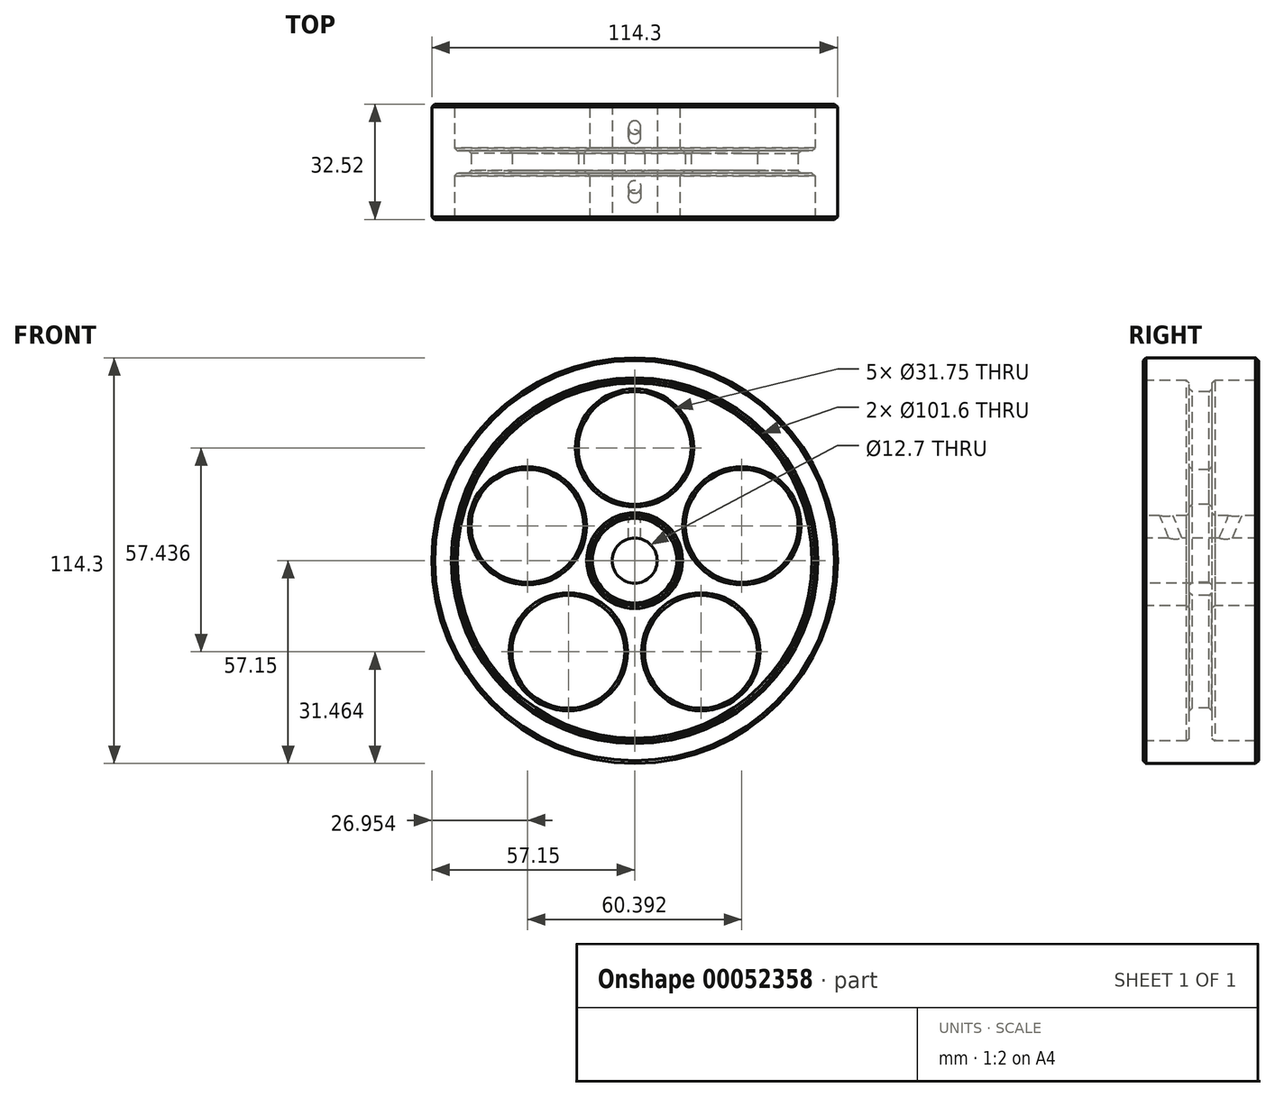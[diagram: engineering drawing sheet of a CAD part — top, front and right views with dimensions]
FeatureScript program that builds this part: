
annotation { "Feature Type Name" : "Feature", "Feature Type Description" : "" }
export const myFeature = defineFeature(function(context is Context, id is Id, definition is map)
    precondition{}
    {
        {
            var Q0;
            Q0=qCreatedBy(makeId("Right.planeOp"),FACE);
            var sketch = newSketch(context, id + "F0", { "sketchPlane" : qUnion([Q0])});
            skLineSegment(sketch, "E0", {"start": v(-16.26, 6.35) * mm, "end": v(-16.26, 12.7) * mm});
            skLineSegment(sketch, "E1", {"start": v(-16.26, 12.7) * mm, "end": v(-3.17, 12.7) * mm});
            skLineSegment(sketch, "E2", {"start": v(-3.17, 12.7) * mm, "end": v(-3.18, 50.8) * mm});
            skLineSegment(sketch, "E3", {"start": v(-3.18, 50.8) * mm, "end": v(-16.26, 50.8) * mm});
            skLineSegment(sketch, "E4", {"start": v(-16.26, 50.8) * mm, "end": v(-16.26, 57.15) * mm});
            skLineSegment(sketch, "E5", {"start": v(-16.26, 57.15) * mm, "end": v(16.26, 57.15) * mm});
            skLineSegment(sketch, "E6", {"start": v(16.26, 57.15) * mm, "end": v(16.26, 50.8) * mm});
            skLineSegment(sketch, "E7", {"start": v(16.26, 50.8) * mm, "end": v(3.17, 50.8) * mm});
            skLineSegment(sketch, "E8", {"start": v(3.17, 50.8) * mm, "end": v(3.18, 12.7) * mm});
            skLineSegment(sketch, "E9", {"start": v(3.18, 12.7) * mm, "end": v(16.26, 12.7) * mm});
            skLineSegment(sketch, "E10", {"start": v(16.26, 12.7) * mm, "end": v(16.26, 6.35) * mm});
            skLineSegment(sketch, "E11", {"start": v(16.26, 6.35) * mm, "end": v(-16.26, 6.35) * mm});
            skLineSegment(sketch, "E12", {"start": v(-16.39, 0) * mm, "end": v(18.55, 0) * mm, "construction": true});
            skPoint(sketch, "E13", {"position": v(0, 57.15) * mm});
            skPoint(sketch, "E14", {"position": v(-9.72, 12.7) * mm});
            skPoint(sketch, "E15", {"position": v(9.72, 12.7) * mm});
            skSolve(sketch);
        }
        {
            var Q0;
            Q0 = qSketchRegion(id + "F0", true);
            var Q1;
            Q1=sQuery(id+"F0.wireOp",EDGE,"E12");
            revolve(context, id + "F1", {"entities" : qUnion([Q0]), "axis" : qUnion([Q1]), "revolveType" : RevolveType.FULL});
        }
        {
            var Q0;
            Q0=qCreatedBy(makeId("Front.planeOp"),FACE);
            var sketch = newSketch(context, id + "F2", { "sketchPlane" : qUnion([Q0])});
            skCircle(sketch, "E16", {"center": v(0, 31.75) * mm, "radius": 15.88 * mm});
            skCircle(sketch, "E17.1.0", {"center": v(-30.2, 9.81) * mm, "radius": 15.88 * mm});
            skCircle(sketch, "E17.2.0", {"center": v(-18.66, -25.69) * mm, "radius": 15.88 * mm});
            skCircle(sketch, "E17.3.0", {"center": v(18.66, -25.69) * mm, "radius": 15.88 * mm});
            skCircle(sketch, "E17.4.0", {"center": v(30.2, 9.81) * mm, "radius": 15.88 * mm});
            skPoint(sketch, "E17.center", {"position": v(0, 0) * mm});
            skCircle(sketch, "E18", {"center": v(0, 0) * mm, "radius": 31.75 * mm, "construction": true});
            skSolve(sketch);
        }
        {
            var Q0;
            Q0 = qSketchRegion(id + "F2", true);
            extrude(context, id + "F3", {"entities" : qUnion([Q0]), "operationType" : NewBodyOperationType.REMOVE, "oppositeDirection" : true, "depth" : 50.8 * mm, "symmetric" : true});
        }
        {
            var Q0;
            Q0=qCreatedBy(makeId("Top.planeOp"),FACE);
            var sketch = newSketch(context, id + "F4", { "sketchPlane" : qUnion([Q0])});
            skLineSegment(sketch, "E19", {"start": v(-62.2, -50.8) * mm, "end": v(72.14, -50.8) * mm, "construction": true});
            skLineSegment(sketch, "E20", {"start": v(-62.2, 50.8) * mm, "end": v(72.14, 50.8) * mm, "construction": true});
            skSolve(sketch);
        }
        {
            var Q0;
            Q0=sQuery(id+"F4.wireOp",EDGE,"E19");
            cPlane(context, id + "F5", {"entities" : qUnion([Q0]), "cplaneType" : CPlaneType.LINE_ANGLE, "offset" : 152.4 * mm, "angle" : 292.5 * degree, "width" : 152.4 * mm, "height" : 152.4 * mm});
        }
        {
            var Q0;
            Q0=sQuery(id+"F4.wireOp",EDGE,"E20");
            cPlane(context, id + "F6", {"entities" : qUnion([Q0]), "cplaneType" : CPlaneType.LINE_ANGLE, "offset" : 152.4 * mm, "angle" : 67.5 * degree, "width" : 152.4 * mm, "height" : 152.4 * mm});
        }
        {
            var Q0;
            Q0=qCreatedBy(id+"F5.planeOp",FACE);
            var sketch = newSketch(context, id + "F7", { "sketchPlane" : qUnion([Q0])});
            skCircle(sketch, "E21", {"center": v(0, 4.12) * mm, "radius": 1.73 * mm});
            skSolve(sketch);
        }
        {
            var Q0;
            Q0 = qSketchRegion(id + "F7", true);
            var Q1;
            Q1=makeQuery(id+"F1.opRevolve","SWEPT_FACE",FACE,{"disambiguationData":[OSD([sQuery(id+"F0.wireOp",EDGE,"E11")])]});
            extrude(context, id + "F8", {"entities" : qUnion([Q0]), "operationType" : NewBodyOperationType.REMOVE, "endBound" : BoundingType.UP_TO_SURFACE, "endBoundEntityFace" : qUnion([Q1]), "depth" : 25.4 * mm});
        }
        {
            var Q0;
            Q0=qCreatedBy(id+"F6.planeOp",FACE);
            var sketch = newSketch(context, id + "F9", { "sketchPlane" : qUnion([Q0])});
            skCircle(sketch, "E22", {"center": v(0, 4.12) * mm, "radius": 1.73 * mm});
            skSolve(sketch);
        }
        {
            var Q0;
            Q0 = qSketchRegion(id + "F9", true);
            var Q1;
            Q1=makeQuery(id+"F1.opRevolve","SWEPT_FACE",FACE,{"disambiguationData":[OSD([sQuery(id+"F0.wireOp",EDGE,"E11")])]});
            extrude(context, id + "F10", {"entities" : qUnion([Q0]), "operationType" : NewBodyOperationType.REMOVE, "endBound" : BoundingType.UP_TO_SURFACE, "oppositeDirection" : true, "endBoundEntityFace" : qUnion([Q1]), "depth" : 25.4 * mm});
        }
        {
            var Q0;
            Q0=makeQuery(id+"F1.opRevolve","SWEPT_EDGE",EDGE,{"disambiguationData":[OSD([sQuery(id+"F0.wireOp",EDGE,"E4"),sQuery(id+"F0.wireOp",EDGE,"E5")])]});
            var Q1;
            Q1=makeQuery(id+"F1.opRevolve","SWEPT_EDGE",EDGE,{"disambiguationData":[OSD([sQuery(id+"F0.wireOp",EDGE,"E5"),sQuery(id+"F0.wireOp",EDGE,"E6")])]});
            var Q2;
            Q2=makeQuery(id+"F1.opRevolve","SWEPT_EDGE",EDGE,{"disambiguationData":[OSD([sQuery(id+"F0.wireOp",EDGE,"E3"),sQuery(id+"F0.wireOp",EDGE,"E4")])]});
            var Q3;
            Q3=makeQuery(id+"F1.opRevolve","SWEPT_EDGE",EDGE,{"disambiguationData":[OSD([sQuery(id+"F0.wireOp",EDGE,"E2"),sQuery(id+"F0.wireOp",EDGE,"E3")])]});
            var Q4;
            Q4=makeQuery(id+"F1.opRevolve","SWEPT_EDGE",EDGE,{"disambiguationData":[OSD([sQuery(id+"F0.wireOp",EDGE,"E6"),sQuery(id+"F0.wireOp",EDGE,"E7")])]});
            var Q5;
            Q5=makeQuery(id+"F1.opRevolve","SWEPT_EDGE",EDGE,{"disambiguationData":[OSD([sQuery(id+"F0.wireOp",EDGE,"E7"),sQuery(id+"F0.wireOp",EDGE,"E8")])]});
            var Q6;
            Q6=makeQuery(id+"F1.opRevolve","SWEPT_EDGE",EDGE,{"disambiguationData":[OSD([sQuery(id+"F0.wireOp",EDGE,"E9"),sQuery(id+"F0.wireOp",EDGE,"E10")])]});
            var Q7;
            Q7=makeQuery(id+"F1.opRevolve","SWEPT_EDGE",EDGE,{"disambiguationData":[OSD([sQuery(id+"F0.wireOp",EDGE,"E8"),sQuery(id+"F0.wireOp",EDGE,"E9")])]});
            var Q8;
            Q8=makeQuery(id+"F1.opRevolve","SWEPT_EDGE",EDGE,{"disambiguationData":[OSD([sQuery(id+"F0.wireOp",EDGE,"E0"),sQuery(id+"F0.wireOp",EDGE,"E1")])]});
            var Q9;
            Q9=makeQuery(id+"F1.opRevolve","SWEPT_EDGE",EDGE,{"disambiguationData":[OSD([sQuery(id+"F0.wireOp",EDGE,"E1"),sQuery(id+"F0.wireOp",EDGE,"E2")])]});
            var Q10;
            Q10=makeQuery(id+"F3.boolean.opBoolean","INTERSECT",EDGE,{"derivedFrom":[makeQuery(id+"F1.opRevolve","SWEPT_FACE",FACE,{"disambiguationData":[OSD([sQuery(id+"F0.wireOp",EDGE,"E2")])]}),makeQuery(id+"F3.opExtrude","SWEPT_FACE",FACE,{"disambiguationData":[OSD([sQuery(id+"F2.wireOp",EDGE,"E16")])]})]});
            var Q11;
            Q11=makeQuery(id+"F3.boolean.opBoolean","INTERSECT",EDGE,{"derivedFrom":[makeQuery(id+"F1.opRevolve","SWEPT_FACE",FACE,{"disambiguationData":[OSD([sQuery(id+"F0.wireOp",EDGE,"E2")])]}),makeQuery(id+"F3.opExtrude","SWEPT_FACE",FACE,{"disambiguationData":[OSD([sQuery(id+"F2.wireOp",EDGE,"E17.4.0")])]})]});
            var Q12;
            Q12=makeQuery(id+"F3.boolean.opBoolean","INTERSECT",EDGE,{"derivedFrom":[makeQuery(id+"F1.opRevolve","SWEPT_FACE",FACE,{"disambiguationData":[OSD([sQuery(id+"F0.wireOp",EDGE,"E2")])]}),makeQuery(id+"F3.opExtrude","SWEPT_FACE",FACE,{"disambiguationData":[OSD([sQuery(id+"F2.wireOp",EDGE,"E17.3.0")])]})]});
            var Q13;
            Q13=makeQuery(id+"F3.boolean.opBoolean","INTERSECT",EDGE,{"derivedFrom":[makeQuery(id+"F1.opRevolve","SWEPT_FACE",FACE,{"disambiguationData":[OSD([sQuery(id+"F0.wireOp",EDGE,"E2")])]}),makeQuery(id+"F3.opExtrude","SWEPT_FACE",FACE,{"disambiguationData":[OSD([sQuery(id+"F2.wireOp",EDGE,"E17.2.0")])]})]});
            var Q14;
            Q14=makeQuery(id+"F3.boolean.opBoolean","INTERSECT",EDGE,{"derivedFrom":[makeQuery(id+"F1.opRevolve","SWEPT_FACE",FACE,{"disambiguationData":[OSD([sQuery(id+"F0.wireOp",EDGE,"E2")])]}),makeQuery(id+"F3.opExtrude","SWEPT_FACE",FACE,{"disambiguationData":[OSD([sQuery(id+"F2.wireOp",EDGE,"E17.1.0")])]})]});
            var Q15;
            Q15=makeQuery(id+"F3.boolean.opBoolean","INTERSECT",EDGE,{"derivedFrom":[makeQuery(id+"F1.opRevolve","SWEPT_FACE",FACE,{"disambiguationData":[OSD([sQuery(id+"F0.wireOp",EDGE,"E8")])]}),makeQuery(id+"F3.opExtrude","SWEPT_FACE",FACE,{"disambiguationData":[OSD([sQuery(id+"F2.wireOp",EDGE,"E16")])]})]});
            var Q16;
            Q16=makeQuery(id+"F3.boolean.opBoolean","INTERSECT",EDGE,{"derivedFrom":[makeQuery(id+"F1.opRevolve","SWEPT_FACE",FACE,{"disambiguationData":[OSD([sQuery(id+"F0.wireOp",EDGE,"E8")])]}),makeQuery(id+"F3.opExtrude","SWEPT_FACE",FACE,{"disambiguationData":[OSD([sQuery(id+"F2.wireOp",EDGE,"E17.1.0")])]})]});
            var Q17;
            Q17=makeQuery(id+"F3.boolean.opBoolean","INTERSECT",EDGE,{"derivedFrom":[makeQuery(id+"F1.opRevolve","SWEPT_FACE",FACE,{"disambiguationData":[OSD([sQuery(id+"F0.wireOp",EDGE,"E8")])]}),makeQuery(id+"F3.opExtrude","SWEPT_FACE",FACE,{"disambiguationData":[OSD([sQuery(id+"F2.wireOp",EDGE,"E17.2.0")])]})]});
            var Q18;
            Q18=makeQuery(id+"F3.boolean.opBoolean","INTERSECT",EDGE,{"derivedFrom":[makeQuery(id+"F1.opRevolve","SWEPT_FACE",FACE,{"disambiguationData":[OSD([sQuery(id+"F0.wireOp",EDGE,"E8")])]}),makeQuery(id+"F3.opExtrude","SWEPT_FACE",FACE,{"disambiguationData":[OSD([sQuery(id+"F2.wireOp",EDGE,"E17.3.0")])]})]});
            var Q19;
            Q19=makeQuery(id+"F3.boolean.opBoolean","INTERSECT",EDGE,{"derivedFrom":[makeQuery(id+"F1.opRevolve","SWEPT_FACE",FACE,{"disambiguationData":[OSD([sQuery(id+"F0.wireOp",EDGE,"E8")])]}),makeQuery(id+"F3.opExtrude","SWEPT_FACE",FACE,{"disambiguationData":[OSD([sQuery(id+"F2.wireOp",EDGE,"E17.4.0")])]})]});
            chamfer(context, id + "F11", {"entities" : qUnion([Q0, Q1, Q2, Q3, Q4, Q5, Q6, Q7, Q8, Q9, Q10, Q11, Q12, Q13, Q14, Q15, Q16, Q17, Q18, Q19]), "width" : 0.8 * mm, "tangentPropagation" : true});
        }
    });
